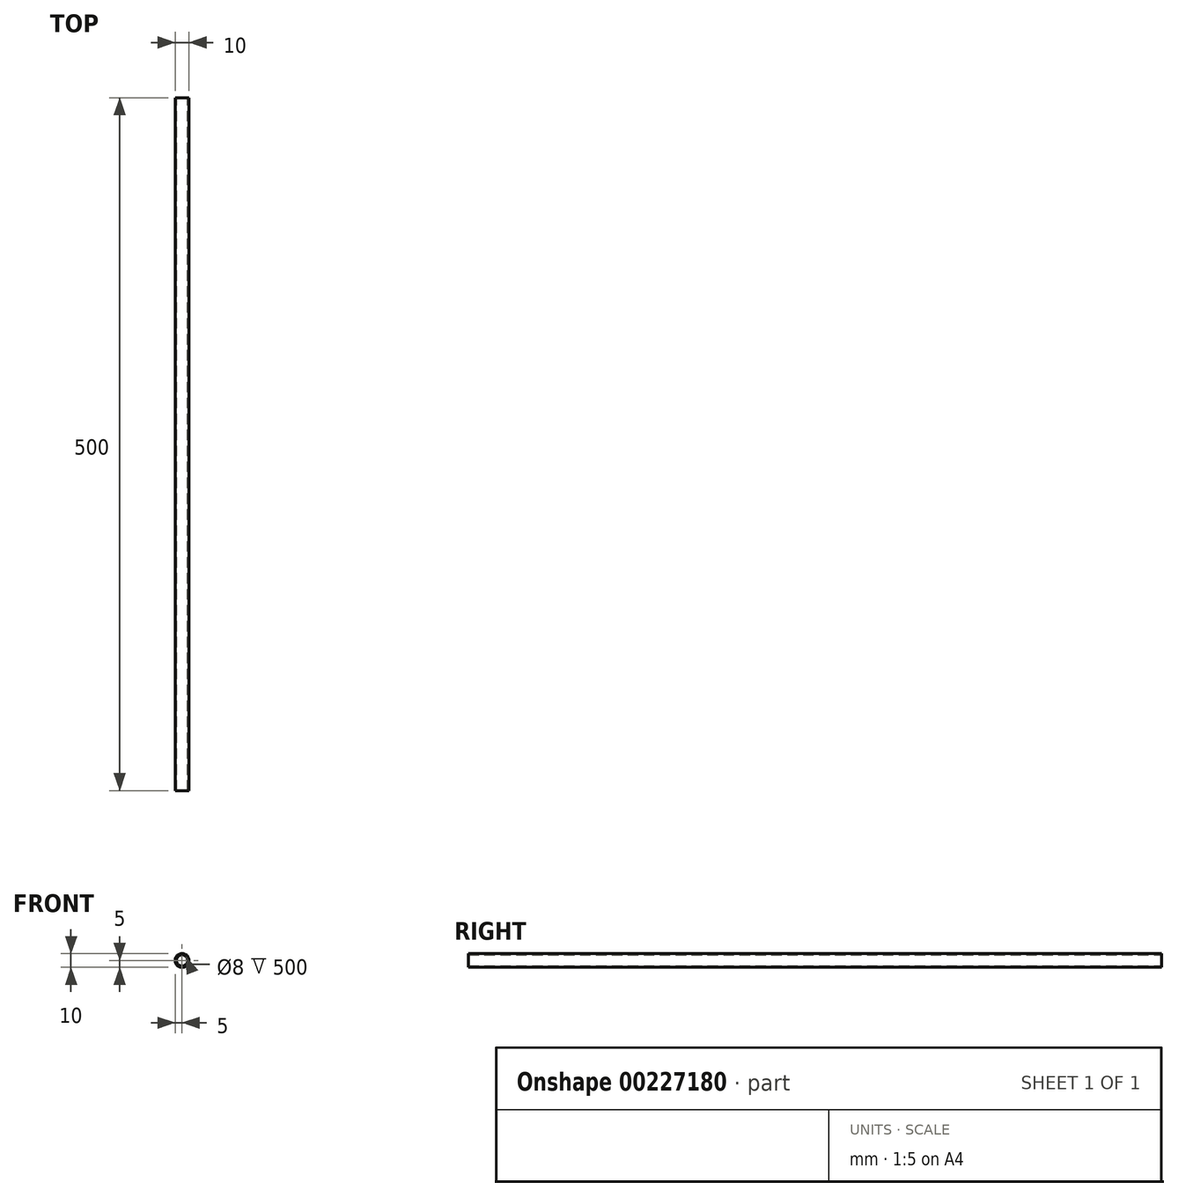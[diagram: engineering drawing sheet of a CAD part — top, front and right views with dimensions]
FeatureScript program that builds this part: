
annotation { "Feature Type Name" : "Feature", "Feature Type Description" : "" }
export const myFeature = defineFeature(function(context is Context, id is Id, definition is map)
    precondition{}
    {
        {
            var Q0;
            Q0=qCreatedBy(makeId("Front.planeOp"),FACE);
            var sketch = newSketch(context, id + "F0", { "sketchPlane" : qUnion([Q0])});
            skCircle(sketch, "E0", {"center": v(0, 0) * mm, "radius": 5 * mm});
            skCircle(sketch, "E1", {"center": v(0, 0) * mm, "radius": 4 * mm});
            skSolve(sketch);
        }
        {
            var Q0;
            Q0 = qSketchRegion(id + "F0", true);
            extrude(context, id + "F1", {"entities" : qUnion([Q0]), "endBound" : BoundingType.SYMMETRIC, "depth" : 500 * mm});
        }
    });
